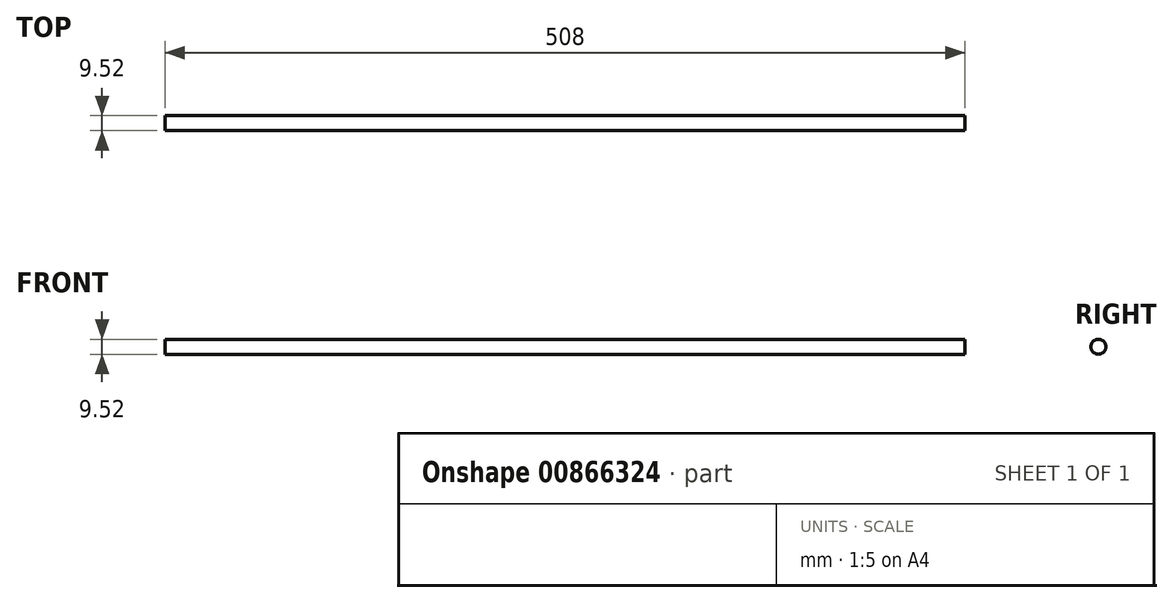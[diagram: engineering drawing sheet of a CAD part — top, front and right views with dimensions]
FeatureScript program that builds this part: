
annotation { "Feature Type Name" : "Feature", "Feature Type Description" : "" }
export const myFeature = defineFeature(function(context is Context, id is Id, definition is map)
    precondition{}
    {
        {
            var Q0;
            Q0=qCreatedBy(makeId("Right.planeOp"),FACE);
            var sketch = newSketch(context, id + "F0", { "sketchPlane" : qUnion([Q0])});
            skCircle(sketch, "E0", {"center": v(0, 0) * mm, "radius": 4.76 * mm});
            skSolve(sketch);
        }
        {
            var Q0;
            Q0 = qSketchRegion(id + "F0", true);
            extrude(context, id + "F1", {"entities" : qUnion([Q0]), "endBound" : BoundingType.SYMMETRIC, "depth" : 508 * mm, "offsetDistance" : 25.4 * mm});
        }
    });
